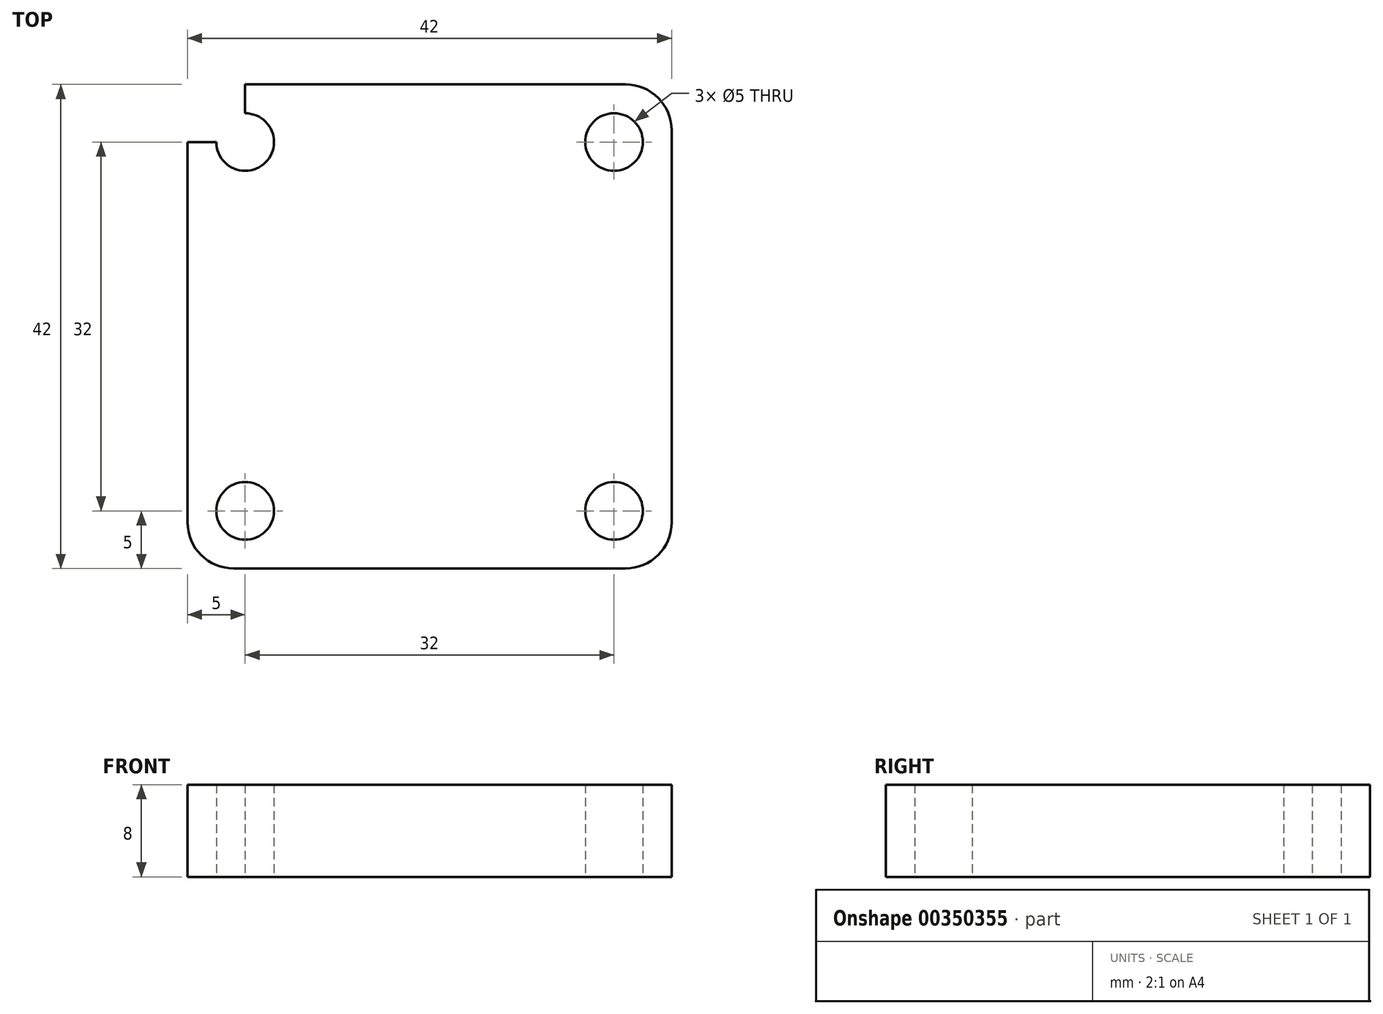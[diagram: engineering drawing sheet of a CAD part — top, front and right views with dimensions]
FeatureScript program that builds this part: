
annotation { "Feature Type Name" : "Feature", "Feature Type Description" : "" }
export const myFeature = defineFeature(function(context is Context, id is Id, definition is map)
    precondition{}
    {
        {
            var Q0;
            Q0=qCreatedBy(makeId("Top.planeOp"),FACE);
            var sketch = newSketch(context, id + "F0", { "sketchPlane" : qUnion([Q0])});
            skLineSegment(sketch, "E0.bottom", {"start": v(21, -21) * mm, "end": v(-21, -21) * mm});
            skLineSegment(sketch, "E0.top", {"start": v(21, 21) * mm, "end": v(-21, 21) * mm});
            skLineSegment(sketch, "E0.left", {"start": v(21, -21) * mm, "end": v(21, 21) * mm});
            skLineSegment(sketch, "E0.right", {"start": v(-21, -21) * mm, "end": v(-21, 21) * mm});
            skPoint(sketch, "E0.middle", {"position": v(0, 0) * mm});
            skLineSegment(sketch, "E1.bottom", {"start": v(-21, 21) * mm, "end": v(-16, 21) * mm});
            skLineSegment(sketch, "E1.top", {"start": v(-21, 16) * mm, "end": v(-16, 16) * mm});
            skLineSegment(sketch, "E1.left", {"start": v(-21, 21) * mm, "end": v(-21, 16) * mm});
            skLineSegment(sketch, "E1.right", {"start": v(-16, 21) * mm, "end": v(-16, 16) * mm});
            skCircle(sketch, "E2", {"center": v(-16, 16) * mm, "radius": 2.5 * mm});
            skCircle(sketch, "E3.1.0", {"center": v(-16, -16) * mm, "radius": 2.5 * mm});
            skCircle(sketch, "E3.2.0", {"center": v(16, -16) * mm, "radius": 2.5 * mm});
            skCircle(sketch, "E3.3.0", {"center": v(16, 16) * mm, "radius": 2.5 * mm});
            skSolve(sketch);
        }
        {
            var Q0;
            {var subQ1=sQuery(id+"F0.wireOp",EDGE,"E1.bottom");Q0=makeQuery(id+"F0.imprint","IMPRINT",FACE,{"disambiguationData":[TD([[makeQuery(id+"F0.imprint","IMPRINT",EDGE,{"derivedFrom":subQ1}),-1.0]])]});}
            var Q1;
            Q1=makeQuery(id+"F0.imprint","IMPRINT",FACE,{"disambiguationData":[TD([[makeQuery(id+"F0.imprint","IMPRINT",EDGE,{"derivedFrom":sQuery(id+"F0.wireOp",EDGE,"E0.bottom")}),-1.0]])]});
            extrude(context, id + "F1", {"entities" : qUnion([Q0, Q1]), "depth" : 8 * mm});
        }
        {
            var Q0;
            Q0=makeQuery(id+"F1.opExtrude","SWEPT_EDGE",EDGE,{"disambiguationData":[OSD([sQuery(id+"F0.wireOp",EDGE,"E0.bottom"),sQuery(id+"F0.wireOp",EDGE,"E0.left")])]});
            var Q1;
            Q1=makeQuery(id+"F1.opExtrude","SWEPT_EDGE",EDGE,{"disambiguationData":[OSD([sQuery(id+"F0.wireOp",EDGE,"E0.bottom"),sQuery(id+"F0.wireOp",EDGE,"E0.right")])]});
            var Q2;
            Q2=makeQuery(id+"F1.opExtrude","SWEPT_EDGE",EDGE,{"disambiguationData":[OSD([sQuery(id+"F0.wireOp",EDGE,"E0.top"),sQuery(id+"F0.wireOp",EDGE,"E0.left")])]});
            var Q3;
            Q3=makeQuery(id+"F1.opExtrude","SWEPT_EDGE",EDGE,{"disambiguationData":[OSD([sQuery(id+"F0.wireOp",EDGE,"E1.bottom"),sQuery(id+"F0.wireOp",EDGE,"E1.left")])]});
            fillet(context, id + "F2", {"entities" : qUnion([Q0, Q1, Q2, Q3]), "radius" : 4 * mm, "tangentPropagation" : true, "allowEdgeOverflow" : false});
        }
    });
